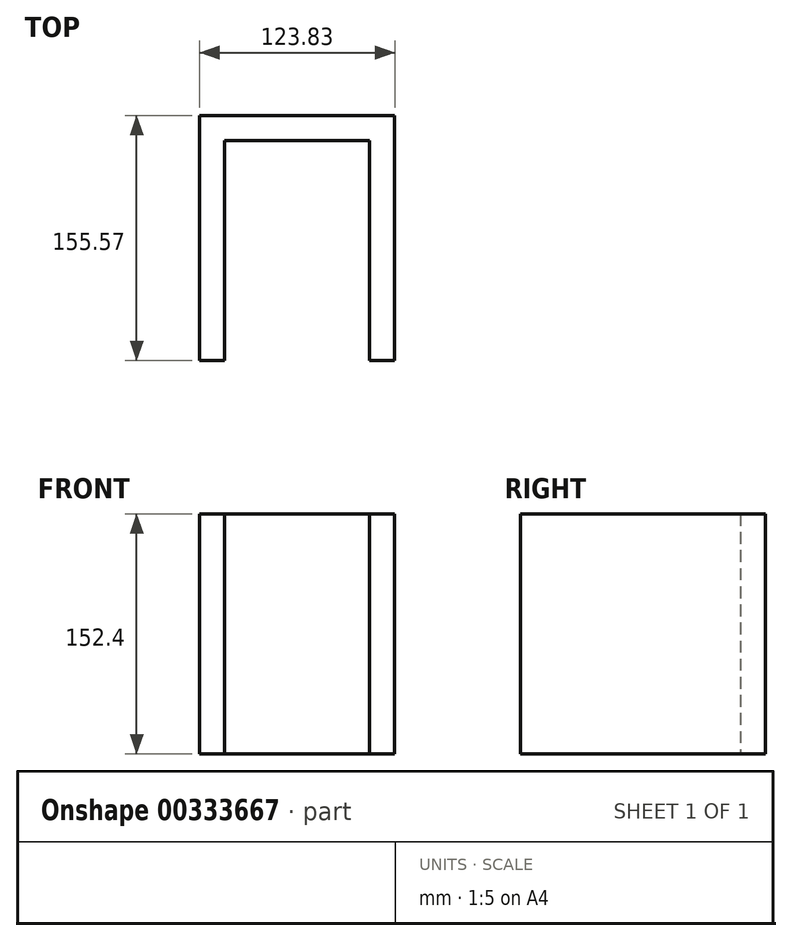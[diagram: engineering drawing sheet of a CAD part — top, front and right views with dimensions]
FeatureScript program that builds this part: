
annotation { "Feature Type Name" : "Feature", "Feature Type Description" : "" }
export const myFeature = defineFeature(function(context is Context, id is Id, definition is map)
    precondition{}
    {
        {
            var Q0;
            Q0=qCreatedBy(makeId("Top.planeOp"),FACE);
            var sketch = newSketch(context, id + "F0", { "sketchPlane" : qUnion([Q0])});
            skLineSegment(sketch, "E0", {"start": v(0, 0) * mm, "end": v(0, 155.58) * mm});
            skLineSegment(sketch, "E1", {"start": v(0, 155.58) * mm, "end": v(123.82, 155.58) * mm});
            skLineSegment(sketch, "E2", {"start": v(123.83, 155.58) * mm, "end": v(123.83, 0) * mm});
            skLineSegment(sketch, "E3.0", {"start": v(107.95, 139.7) * mm, "end": v(107.95, 0) * mm});
            skLineSegment(sketch, "E3.1", {"start": v(15.88, 139.7) * mm, "end": v(107.95, 139.7) * mm});
            skLineSegment(sketch, "E3.2", {"start": v(15.88, 0) * mm, "end": v(15.88, 139.7) * mm});
            skLineSegment(sketch, "E4", {"start": v(0, 0) * mm, "end": v(15.88, 0) * mm});
            skLineSegment(sketch, "E5", {"start": v(107.95, 0) * mm, "end": v(123.83, 0) * mm});
            skSolve(sketch);
        }
        {
            var Q0;
            Q0=makeQuery(id+"F0.imprint","IMPRINT",FACE,{"disambiguationData":[TD([[makeQuery(id+"F0.imprint","IMPRINT",EDGE,{"derivedFrom":sQuery(id+"F0.wireOp",EDGE,"E0")}),-1.0]])]});
            extrude(context, id + "F1", {"entities" : qUnion([Q0]), "depth" : 152.4 * mm});
        }
    });
